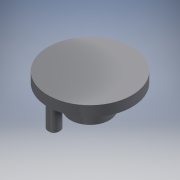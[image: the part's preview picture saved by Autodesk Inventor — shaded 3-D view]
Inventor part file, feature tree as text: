
AUTODESK INVENTOR PART (.ipt)
format: ipt  version: 2016 (Build 200138000, 138)  size: 148,992 bytes
history: native  units: mm
features: plane x4, extrude x4, sketch x3, reference x3, thicken_offset x2, chamfer x1, projected_geometry x1
ambient origin geometry x8: Origin, YZ Plane, XZ Plane, XY Plane, X Axis, Y Axis, Z Axis, Center Point
bodies: Solid1 (feature_tree)
feature tree (18):
  plane  "Work Plane1"
  extrude  "Extrusion1"  Depth=3.0mm TaperAngle=0.0deg
  extrude  "Extrusion2"  Depth=1.0mm TaperAngle=45.0deg
  chamfer  "Chamfer1"  Distance=2.0mm
  sketch  "Sketch3"  dims[d5=6.0mm d7=1.0mm d8=2.0mm d9=45.0deg d10=2.0mm d11=0.0mm]
  plane  "Work Plane2"
  plane  "Work Plane3"
  extrude  "Extrusion3"  Depth=10.0mm
  thicken_offset  "Thicken1"
  thicken_offset  "Thicken2"
  plane  "Work Plane4"
  extrude  "Extrusion5"  Depth=3.0mm
  sketch  "Sketch2"  dims[d1=10.0mm d2=0.0mm d3=3.0mm d4=0.0mm]
  projected_geometry  "Projected Loop2"
  reference  "Reference5"
  reference  "Reference6"
  reference  "Reference7"
  sketch  "Sketch5"  dims[d14=0.1mm d15=0.1mm d17=1.0mm d18=2.0mm d19=3.0mm d20=10.0mm d21=0.0mm d22=41.0mm]
